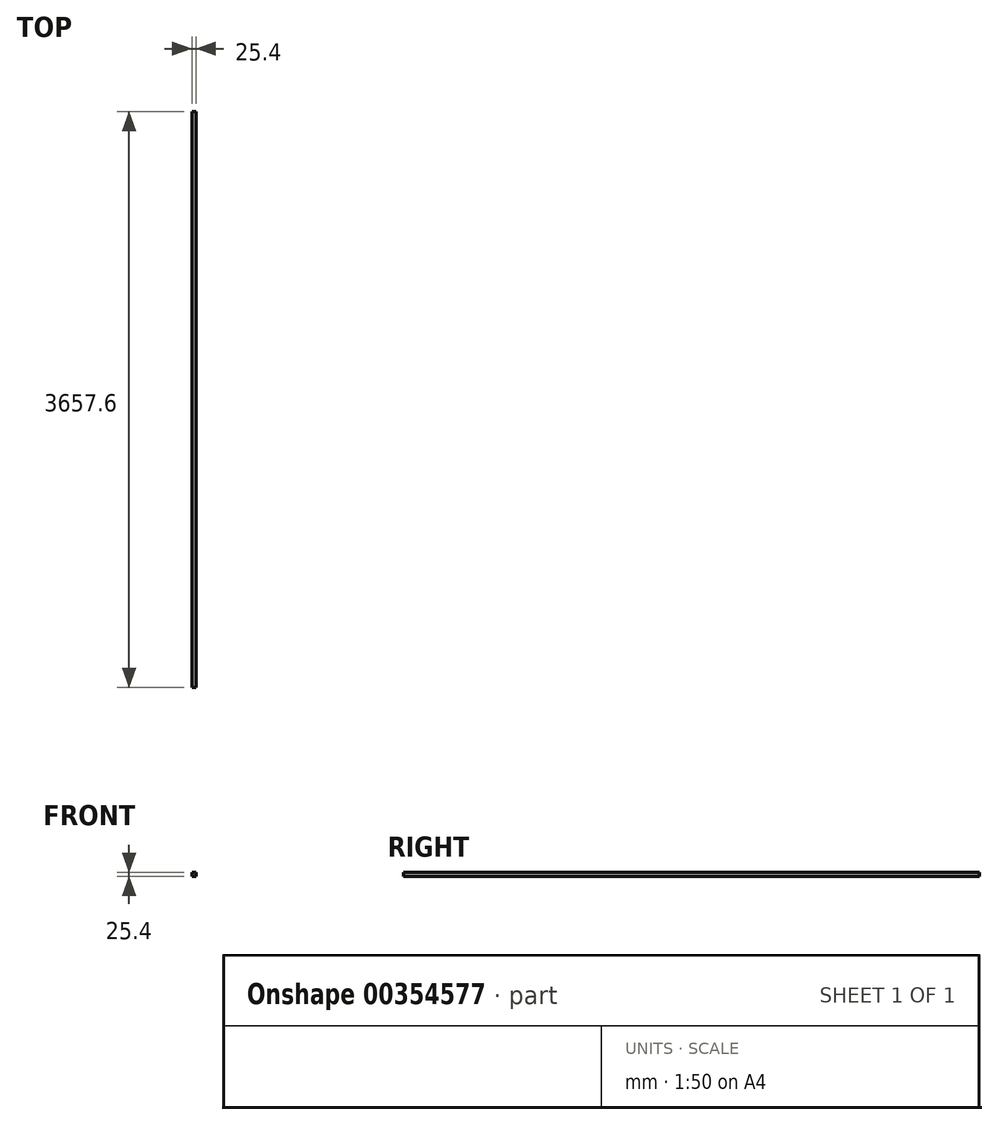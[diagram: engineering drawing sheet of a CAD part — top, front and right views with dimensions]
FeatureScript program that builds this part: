
annotation { "Feature Type Name" : "Feature", "Feature Type Description" : "" }
export const myFeature = defineFeature(function(context is Context, id is Id, definition is map)
    precondition{}
    {
        {
            var Q0;
            Q0=qCreatedBy(makeId("Top.planeOp"),FACE);
            var sketch = newSketch(context, id + "F0", { "sketchPlane" : qUnion([Q0])});
            skLineSegment(sketch, "E0.bottom", {"start": v(-27.15, -13.43) * mm, "end": v(-1.75, -13.43) * mm});
            skLineSegment(sketch, "E0.top", {"start": v(-27.15, 3644.17) * mm, "end": v(-1.75, 3644.17) * mm});
            skLineSegment(sketch, "E0.left", {"start": v(-27.15, -13.43) * mm, "end": v(-27.15, 3644.17) * mm});
            skLineSegment(sketch, "E0.right", {"start": v(-1.75, -13.43) * mm, "end": v(-1.75, 3644.17) * mm});
            skSolve(sketch);
        }
        {
            var Q0;
            Q0=makeQuery(id+"F0.imprint","IMPRINT",FACE,{"disambiguationData":[TD([[makeQuery(id+"F0.imprint","IMPRINT",EDGE,{"derivedFrom":sQuery(id+"F0.wireOp",EDGE,"E0.bottom")}),1.0]])]});
            extrude(context, id + "F1", {"entities" : qUnion([Q0]), "depth" : 25.4 * mm});
        }
    });
